# Revit family: ONRM - 4, 6, 8, 12, - All
name_source: partatom
category: Mechanical Equipment
revit_build: Autodesk Revit 2017 (Build: 20181011_1645(x64)
units: mm (PartAtom-declared; Revit-internal decimal feet)

## family parameters
Always vertical = Yes
Cut with Voids When Loaded = No
OmniClass Number = 23.40.40.11.17
OmniClass Title = Refrigerated Cases
Part Type = Normal
Room Calculation Point = No
Round Connector Dimension = Use Radius
Shared = No
Work Plane-Based = Yes

## types (4) — shared parameters
20" Shelf = No
22" Shelf = Yes
Application Discipline = Meat
Certifications = NSF 7, UL471, CSA
Crossfire/Polaris Amps = 0 A
DATE = 01/29/2016
DESIGNERS NAME = SHIDDRAMESH
Default Elevation = 48"
Defrosts Per Day_2 = 2
Description = Narrow Reach-In Merchandiser
Discharge Air Velocity (FPM) = 380
ENDS = CHARCOAL BROWN
EQUIPMENT DESCRIPTION = Narrow Reach-In Merchandiser
EQUIPMENT MARK = ONRM
FLAT FRONT PANEL = CHARCOAL BROWN
FRAME LENGTH = 0"
GE Immersion Amps = 0 A
GLASS = Glass
Height = 81"
Item Description = Narrow Reach-In Merchandiser
Keynote = ONRM
Legend Number = ONRM
Manufacturer = HILL PHOENIX
Model = ONRM
Size of Door = 24"
TOP OF CASE AND ELECTRICAL BOX = CHARCOAL BROWN
Timed-Off Defrost Fail-Safe (Min) = 30
Timed-Off Defrost Termination Temp_2 = 42
Type of Door Swing = B-Swing
URL = http://www.hillphoenix.com
Width = 34 7/8"

## per-type parameters (varying)
- 06'-32" Door - Beverage: 101 Amps=0 A; 101 Watts=49 W; BTUH Conventional=510; BTUH Parallel=480; BUMPER=<By Category>; CENTER LINE & DRAIN=36"; Crossfire/Polaris Watts=24 W; DOOR CONFIGURATION=MASTER DOOR.0009 : 24" X 64 3/8" 3 DOOR B SWING (LEFT OPENING END); DOOR GLASS MATERIAL=<By Category>; DOOR HANDLE MATERIAL=<By Category>; DOOR MATERIAL=<By Category>; Discharge Air (°F)=38 °F; END TRIM=BLACK PAINTED METAL; Eliminaator Amps=1 A; Eliminaator Watts=135 W; Evaporator (°F)=34 °F; FRAME MATERIAL=<By Category>; GE Immersion Watts=9 W; High Efficiency Amps=0 A; High Efficiency Watts=52 W; INTERIOR=BLACK PAINTED METAL; KICK PLATE=BLACK PAINTED METAL; Length=72"; NUMBER OF DOORS=2; Number of Fans per Case=2; Optimax Pro Amps=0 A; Optimax Pro Watts=58 W; Superheat Set Point @ Bulb (°F)=6-8; Vista Optimax Pro Amps=0 A; Vista Optimax Pro Watts=0 W; Vista-C/60 Amps=1 A; Vista-C/60 Watts=70 W
- 04'-24" Door - Beverage: 101 Amps=0 A; 101 Watts=28 W; BTUH Conventional=510; BTUH Parallel=480; BUMPER=<By Category>; CENTER LINE & DRAIN=24"; Crossfire/Polaris Watts=15 W; DOOR CONFIGURATION=MASTER DOOR.0009 : 24" X 64 3/8" 2 DOOR B SWING; DOOR GLASS MATERIAL=<By Category>; DOOR HANDLE MATERIAL=<By Category>; DOOR MATERIAL=<By Category>; Discharge Air (°F)=32; END TRIM=BLACK PAINTED METAL; Eliminaator Amps=1 A; Eliminaator Watts=135 W; Evaporator (°F)=28; FRAME MATERIAL=<By Category>; GE Immersion Watts=6 W; High Efficiency Amps=0 A; High Efficiency Watts=52 W; INTERIOR=BLACK PAINTED METAL; KICK PLATE=BLACK PAINTED METAL; Length=48"; NUMBER OF DOORS=2; Number of Fans per Case=2; Optimax Pro Amps=0 A; Optimax Pro Watts=58 W; Superheat Set Point @ Bulb (°F)=6 - 8; Vista Optimax Pro Amps=0 A; Vista Optimax Pro Watts=0 W; Vista-C/60 Amps=0 A; Vista-C/60 Watts=52 W
- 08'-24" - Door - Meat 4: 101 Amps=0 A; 101 Watts=56 W; BTUH Conventional=510; BTUH Parallel=480; BUMPER=Porcelain, Linen; CENTER LINE & DRAIN=48"; Crossfire/Polaris Watts=30 W; DOOR CONFIGURATION=MASTER DOOR.0009 : 24" X 64 3/8" 4 DOOR B SWING; DOOR GLASS MATERIAL=Glass; DOOR HANDLE MATERIAL=Porcelain, Linen; DOOR MATERIAL=Porcelain, Linen; Discharge Air (°F)=32; END TRIM=Porcelain, Linen; Eliminaator Amps=0 A; Eliminaator Watts=0 W; Evaporator (°F)=26; FRAME MATERIAL=Porcelain, Linen; GE Immersion Watts=12 W; High Efficiency Amps=1 A; High Efficiency Watts=79 W; INTERIOR=Porcelain, Linen; KICK PLATE=Porcelain, Linen; Length=96"; NUMBER OF DOORS=4; Number of Fans per Case=3; Optimax Pro Amps=1 A; Optimax Pro Watts=87 W; Superheat Set Point @ Bulb (°F)=6-8; Vista Optimax Pro Amps=1 A; Vista Optimax Pro Watts=63 W; Vista-C/60 Amps=1 A; Vista-C/60 Watts=82 W
- 12'-24" - Door - Beverage: 101 Amps=1 A; 101 Watts=85 W; BTUH Conventional=433; BTUH Parallel=409; BUMPER=<By Category>; CENTER LINE & DRAIN=72"; Crossfire/Polaris Watts=45 W; DOOR CONFIGURATION=MASTER DOOR.0009 : 24" X 64 3/8" 6 DOOR B SWING; DOOR GLASS MATERIAL=<By Category>; DOOR HANDLE MATERIAL=<By Category>; DOOR MATERIAL=<By Category>; Discharge Air (°F)=38 °F; END TRIM=BLACK PAINTED METAL; Eliminaator Amps=2 A; Eliminaator Watts=187 W; Evaporator (°F)=34 °F; FRAME MATERIAL=<By Category>; GE Immersion Watts=18 W; High Efficiency Amps=1 A; High Efficiency Watts=106 W; INTERIOR=BLACK PAINTED METAL; KICK PLATE=BLACK PAINTED METAL; Length=144"; NUMBER OF DOORS=4; Number of Fans per Case=4; Optimax Pro Amps=1 A; Optimax Pro Watts=77 W; Superheat Set Point @ Bulb (°F)=6-8; Vista Optimax Pro Amps=0 A; Vista Optimax Pro Watts=0 W; Vista-C/60 Amps=1 A; Vista-C/60 Watts=112 W

## geometry (parser evidence)
native form markers: Blend x3, Sweep x4
no freeform markers — native parametric forms only
